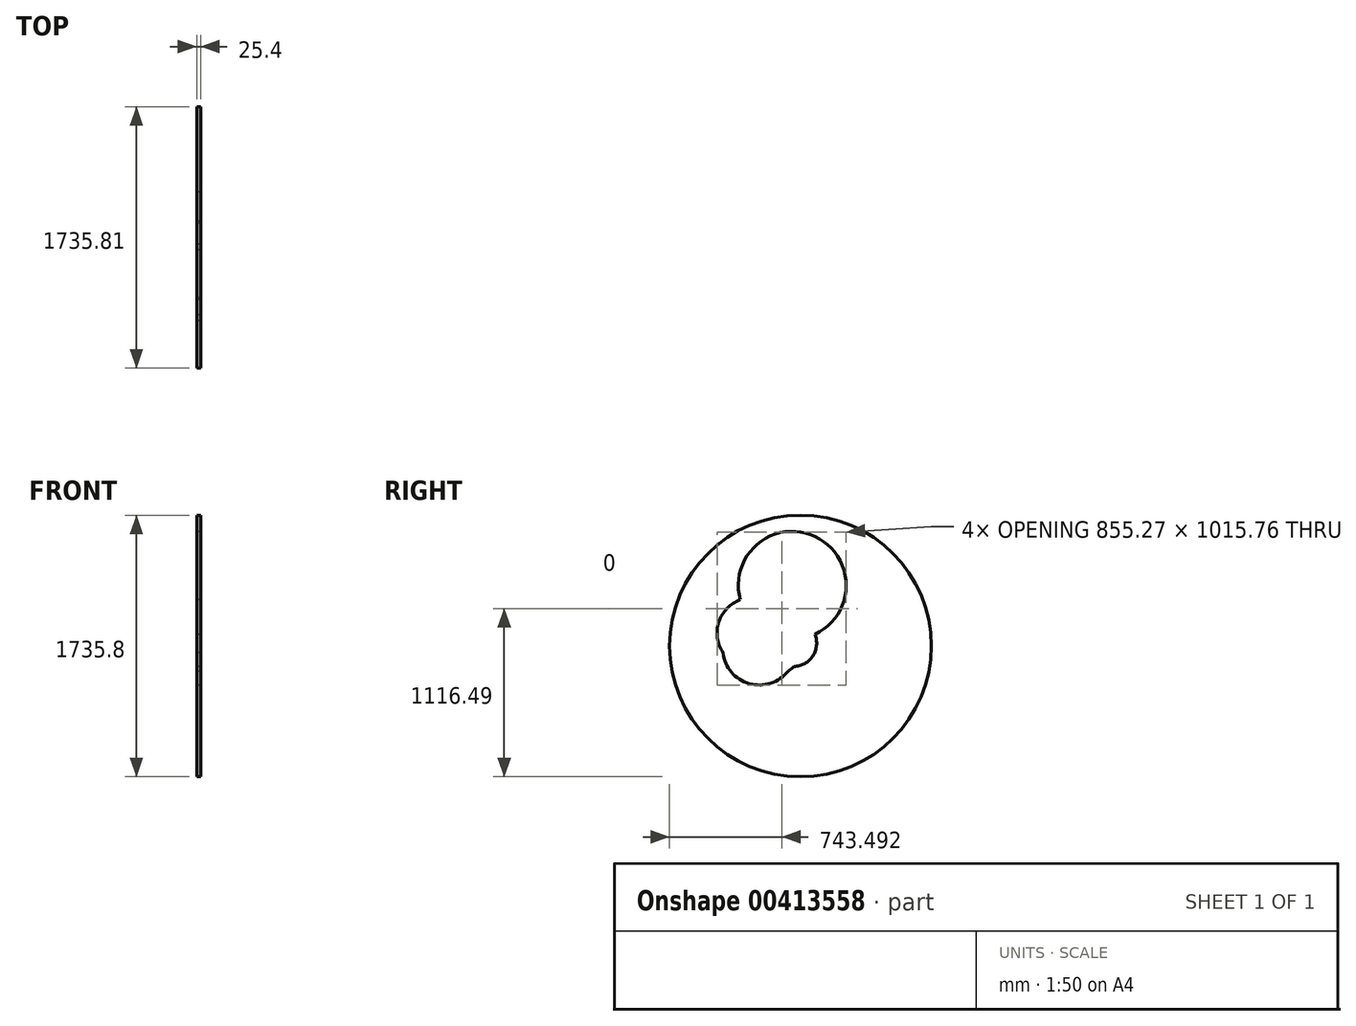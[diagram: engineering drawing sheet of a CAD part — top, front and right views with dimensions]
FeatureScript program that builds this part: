
annotation { "Feature Type Name" : "Feature", "Feature Type Description" : "" }
export const myFeature = defineFeature(function(context is Context, id is Id, definition is map)
    precondition{}
    {
        {
            var Q0;
            Q0=qCreatedBy(makeId("Right.planeOp"),FACE);
            var sketch = newSketch(context, id + "F0", { "sketchPlane" : qUnion([Q0])});
            skCircle(sketch, "E0", {"center": v(2.75, 0) * mm, "radius": 867.9 * mm});
            skCircle(sketch, "E1", {"center": v(-232.6, 45.81) * mm, "radius": 90.02 * mm});
            skCircle(sketch, "E2", {"center": v(-269.62, -15.72) * mm, "radius": 243.6 * mm});
            skCircle(sketch, "E3", {"center": v(-45.37, 18.38) * mm, "radius": 155.45 * mm});
            skCircle(sketch, "E4", {"center": v(-313.56, 85.18) * mm, "radius": 236.73 * mm});
            skCircle(sketch, "E5", {"center": v(-200.62, 26.22) * mm, "radius": 228.61 * mm});
            skCircle(sketch, "E6", {"center": v(-179.43, 97.06) * mm, "radius": 92.6 * mm});
            skCircle(sketch, "E7", {"center": v(-51.78, 401.94) * mm, "radius": 357.75 * mm});
            skSolve(sketch);
        }
        {
            var Q0;
            Q0 = qSketchRegion(id + "F0", true);
            extrude(context, id + "F1", {"entities" : qUnion([Q0]), "depth" : 25.4 * mm});
        }
    });
